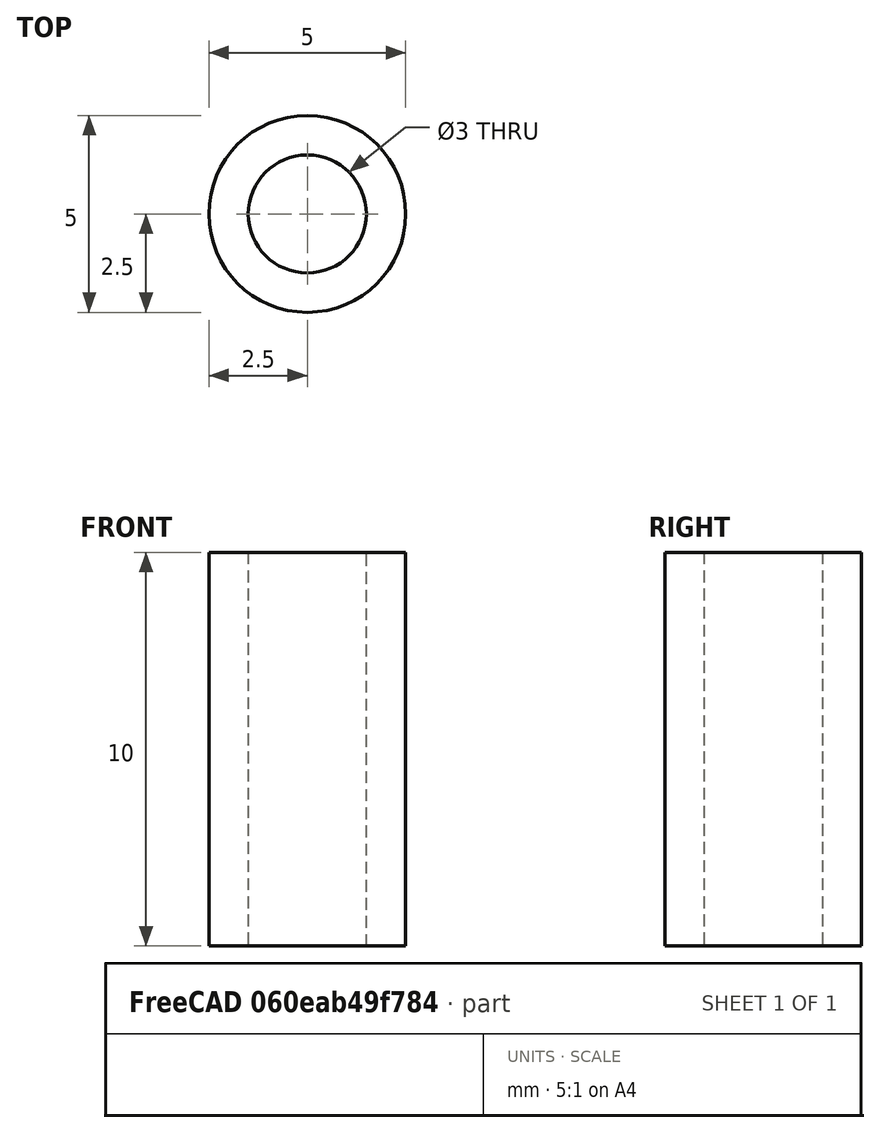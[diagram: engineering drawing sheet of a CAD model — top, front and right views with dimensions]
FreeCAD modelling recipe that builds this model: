
FCSTD DOCUMENT  (FreeCAD 0.18R16146 (Git))
Label: mounts
License: All rights reserved
LicenseURL: http://en.wikipedia.org/wiki/All_rights_reserved
objects: Sketcher::SketchObject×1, PartDesign::Pad×1, PartDesign::Body×1
note: 4 computed .brp shape members not serialized (recipe doc carries the construction recipe); baked Part::Feature solids carry a one-line shape summary decoded from their .brp

FEATURE [Sketcher::SketchObject] Sketch
  MapMode = 5
  Support = -> [XY_Plane]
  sketch-geometry (2):
    g0: Circle CenterX=0 CenterY=0 CenterZ=0 NormalX=0 NormalY=0 NormalZ=1 AngleXU=0 Radius=1.5
    g1: Circle CenterX=0 CenterY=0 CenterZ=0 NormalX=0 NormalY=0 NormalZ=1 AngleXU=0 Radius=2.5
  constraints (4):
    c: Radius(g0) = 1.5
    c: Coincident(g0,g-1)
    c: Coincident(g1,g0)
    c: Radius(g1) = 2.5
FEATURE [PartDesign::Pad] Pad
  Length = 10
  Length2 = 100
  Profile = -> Sketch
  Type = 0
FEATURE [PartDesign::Body] Body
  Group = -> [Sketch,Pad]
  Origin = -> Origin
  Tip = -> Pad
